# Revit family: Water_Heaters_HAJDU_HAJDU-PT-HC-60-F-4+4_
name_source: partatom
category: Mechanical Equipment
units: mm (PartAtom-declared; Revit-internal decimal feet)

## family parameters
Classification = None
Cut with Voids When Loaded = No
Host = Face
Maintain Annotation Orientation = No
OmniClass Number = 23.31.29.13
OmniClass Title = Hot Water Tank Heaters
Part Type = Normal
Room Calculation Point = No
Round Connector Dimension = Use Diameter
Shared = No

## types (1)
- PT HC 60 F 4+4
    Csatlakozó eltolás = 745 mm  [stored 2.44423 ft]
    Default Elevation = 1219 mm
    Description = A PT HC F típusok fűtő- és hűtőrendszerek energiatárolói. Függőleges faltervek. Elsősorban hőszivattyús rendszerekhez ajánlott. A puffertartály acéltartályból, poliuretán hab szigetelésből, fém köpenyből és fedélből áll. 60, 80 és 100 literes 2+2 csonkokban, valamint 60 literes 4+4 csonkban gyártják.
    Energiahatékonysági osztály = B
    Felso csonk = 13 mm
    Hoérzékelo csonk = 13 mm
    Házház anyaga = Hajdu - Felület - Fehér
    Leereszto csonk = 38 mm
    Magasság = 829 mm  [stored 2.71982 ft]
    Manufacturer = HAJDU
    Model = PT HC 60 F 4+4
    Névleges urtartalom = 60 l
    Product Page URL = https://hajdurt.hu
    Tárolási veszteség = 36 W
    Tömeg = 23.00 kg
    URL = https://hajdurt.hu
    Vízcsatlakozás = 38 mm
    Átméro = 450 mm  [stored 1.47638 ft]
    Üzemi nyomás tartály = 0.3 MPa

note: [stored X ft] marks values corroborated as IEEE doubles in the binary element streams (Revit-internal decimal feet)

## geometry (parser evidence)
native form markers: Sweep x6
no freeform markers — native parametric forms only
